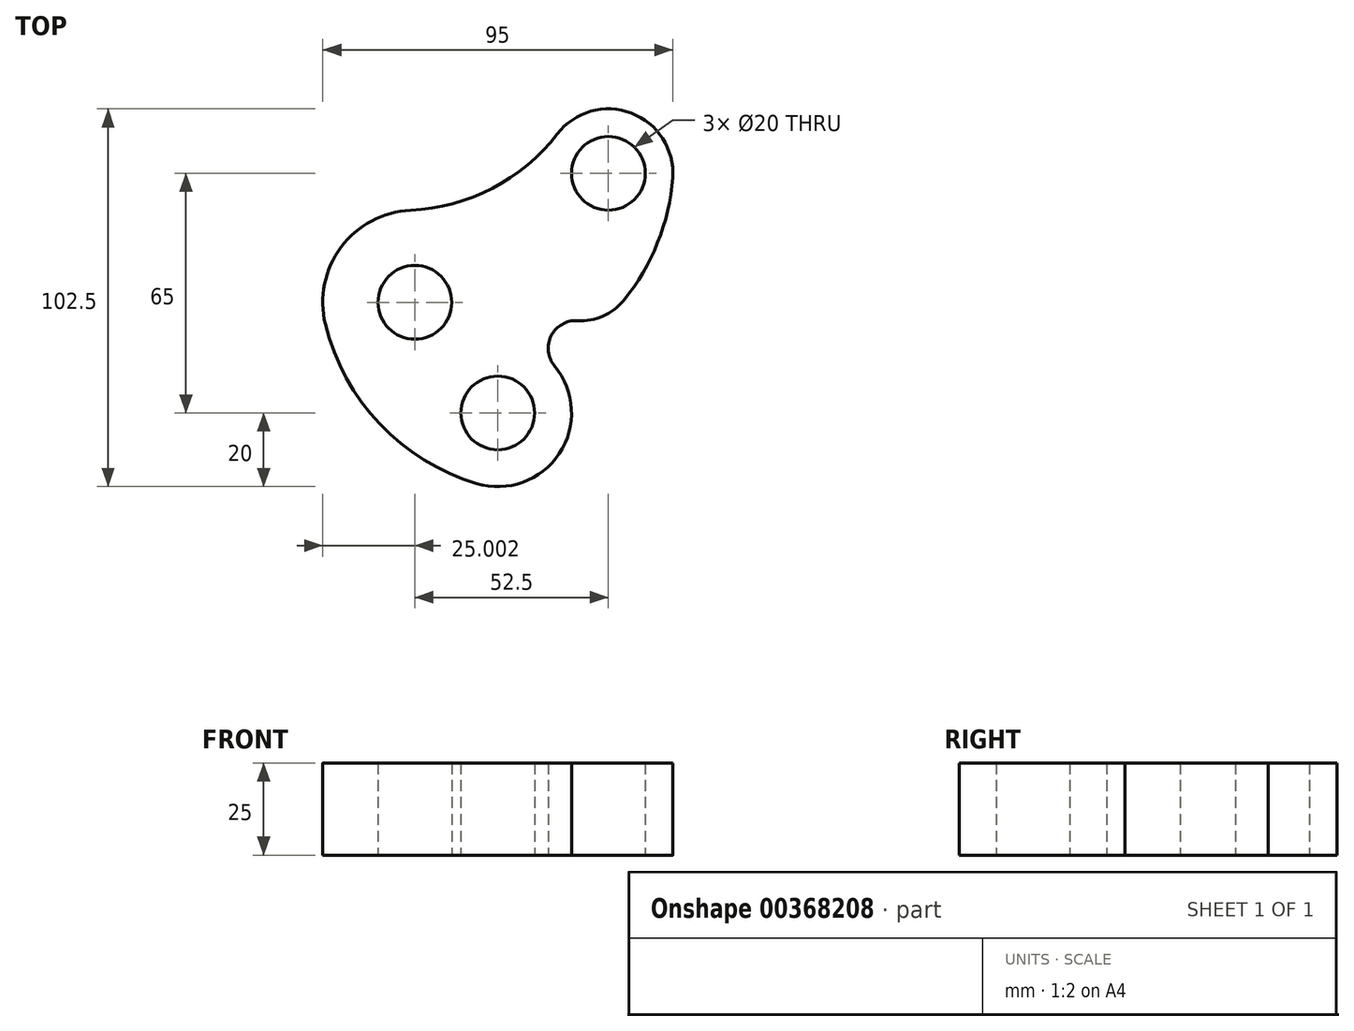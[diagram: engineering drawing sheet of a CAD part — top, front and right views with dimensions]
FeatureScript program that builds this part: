
annotation { "Feature Type Name" : "Feature", "Feature Type Description" : "" }
export const myFeature = defineFeature(function(context is Context, id is Id, definition is map)
    precondition{}
    {
        {
            var Q0;
            Q0=qCreatedBy(makeId("Top.planeOp"),FACE);
            var sketch = newSketch(context, id + "F0", { "sketchPlane" : qUnion([Q0])});
            skCircle(sketch, "E0", {"center": v(-27.34, 0) * mm, "radius": 10 * mm});
            skCircle(sketch, "E1", {"center": v(25.16, 35) * mm, "radius": 10 * mm});
            skCircle(sketch, "E2", {"center": v(-4.84, -30) * mm, "radius": 10 * mm});
            skArc(sketch, "E3", {"start": v(10.57, -17.24) * mm, "mid": v(11.83, -41.05) * mm, "end": v(-10.59, -49.16) * mm});
            skArc(sketch, "E4", {"start": v(10.57, -17.24) * mm, "mid": v(9.65, -9.07) * mm, "end": v(16.78, -4.97) * mm});
            skArc(sketch, "E5", {"start": v(29.28, 0.51) * mm, "mid": v(23.7, -3.73) * mm, "end": v(16.78, -4.97) * mm});
            skArc(sketch, "E6", {"start": v(42.62, 33.86) * mm, "mid": v(38.5, 16.16) * mm, "end": v(29.28, 0.51) * mm});
            skArc(sketch, "E7", {"start": v(42.62, 33.86) * mm, "mid": v(31.35, 51.37) * mm, "end": v(11.3, 45.7) * mm});
            skArc(sketch, "E8", {"start": v(-51.62, -5.94) * mm, "mid": v(-36.85, -33) * mm, "end": v(-10.59, -49.16) * mm});
            skArc(sketch, "E9", {"start": v(-51.62, -5.94) * mm, "mid": v(-47.36, 14.98) * mm, "end": v(-28.5, 24.97) * mm});
            skArc(sketch, "E10", {"start": v(11.3, 45.7) * mm, "mid": v(-6.31, 30.95) * mm, "end": v(-28.5, 24.97) * mm});
            skSolve(sketch);
        }
        {
            var Q0;
            Q0=makeQuery(id+"F0.imprint","IMPRINT",FACE,{"disambiguationData":[TD([[makeQuery(id+"F0.imprint","IMPRINT",EDGE,{"derivedFrom":sQuery(id+"F0.wireOp",EDGE,"E0")}),-1.0]])]});
            extrude(context, id + "F1", {"entities" : qUnion([Q0]), "depth" : 25 * mm});
        }
    });
